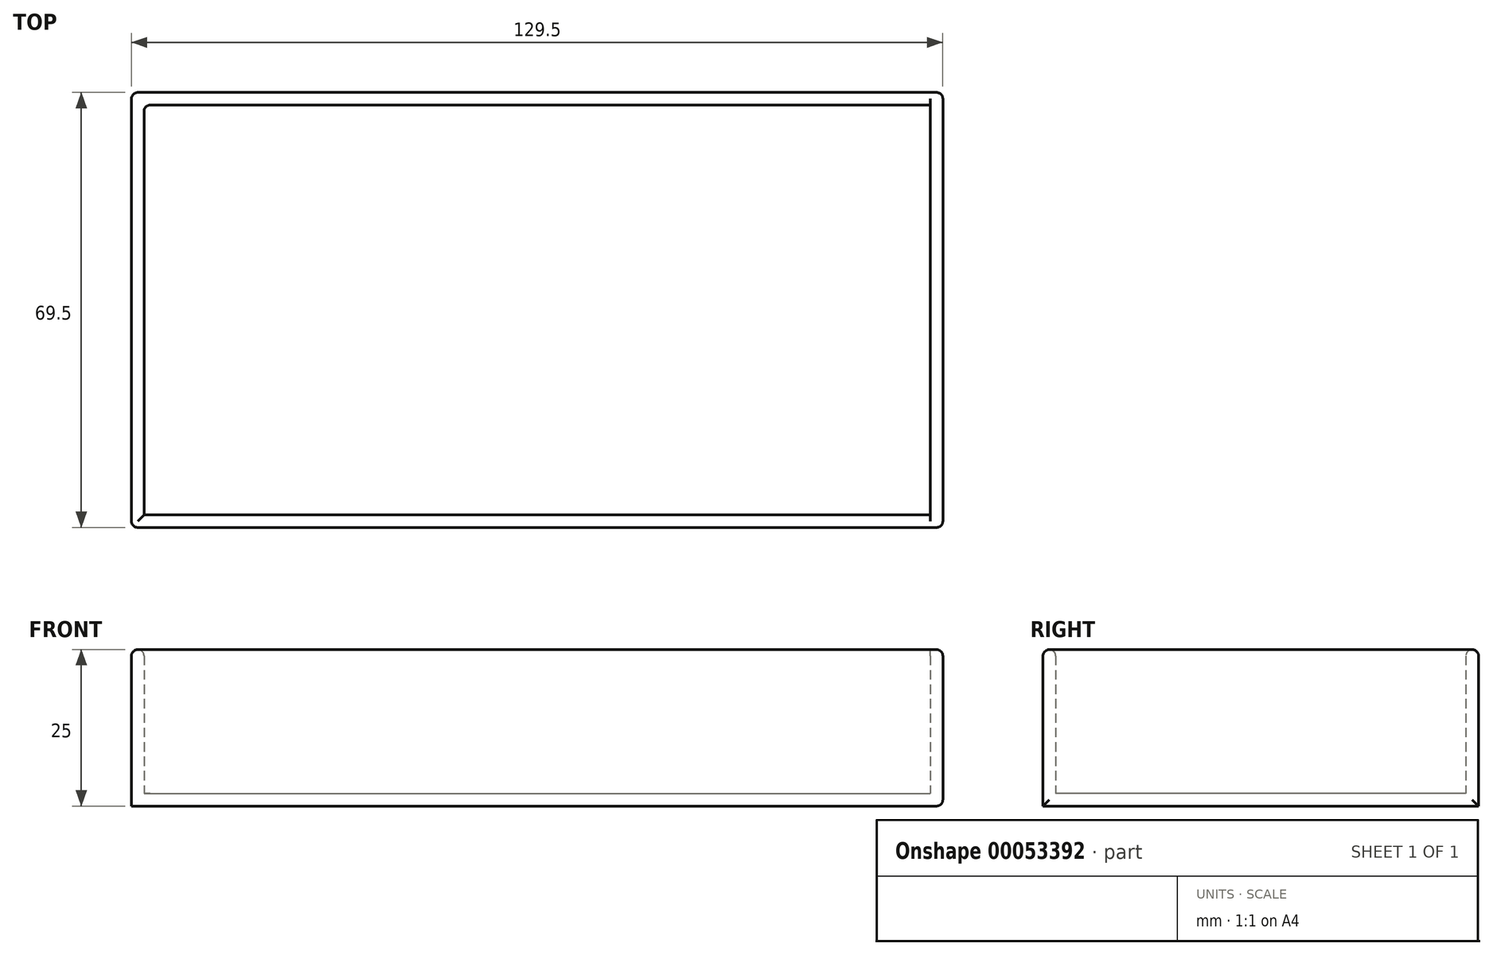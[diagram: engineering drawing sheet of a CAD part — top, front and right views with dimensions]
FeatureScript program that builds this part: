
annotation { "Feature Type Name" : "Feature", "Feature Type Description" : "" }
export const myFeature = defineFeature(function(context is Context, id is Id, definition is map)
    precondition{}
    {
        {
            var Q0;
            Q0=qCreatedBy(makeId("Top.planeOp"),FACE);
            var sketch = newSketch(context, id + "F0", { "sketchPlane" : qUnion([Q0])});
            skLineSegment(sketch, "E0.bottom", {"start": v(-56.56, 28.08) * mm, "end": v(72.94, 28.08) * mm});
            skLineSegment(sketch, "E0.top", {"start": v(-56.56, -41.42) * mm, "end": v(72.94, -41.42) * mm});
            skLineSegment(sketch, "E0.left", {"start": v(-56.56, 28.08) * mm, "end": v(-56.56, -41.42) * mm});
            skLineSegment(sketch, "E0.right", {"start": v(72.94, 28.08) * mm, "end": v(72.94, -41.42) * mm});
            skSolve(sketch);
        }
        {
            var Q0;
            Q0=makeQuery(id+"F0.imprint","IMPRINT",FACE,{"disambiguationData":[TD([[makeQuery(id+"F0.imprint","IMPRINT",EDGE,{"derivedFrom":sQuery(id+"F0.wireOp",EDGE,"E0.bottom")}),-1.0]])]});
            extrude(context, id + "F1", {"entities" : qUnion([Q0]), "depth" : 25 * mm});
        }
        {
            var Q0;
            Q0=makeQuery(id+"F1.opExtrude","CAP_FACE",FACE,{"disambiguationData":[OSD([sQuery(id+"F0.wireOp",EDGE,"E0.bottom"),sQuery(id+"F0.wireOp",EDGE,"E0.top"),sQuery(id+"F0.wireOp",EDGE,"E0.left"),sQuery(id+"F0.wireOp",EDGE,"E0.right")])],"isStart":false});
            shell(context, id + "F2", {"entities" : qUnion([Q0]), "thickness" : 2 * mm});
        }
        {
            var Q0;
            {var subQ0=sQuery(id+"F0.wireOp",EDGE,"E0.bottom");Q0=makeQuery(id+"F2.opShell","OFFSET_EDGE",EDGE,{"disambiguationData":[OSD([subQ0]),TDD([makeQuery(id+"F1.opExtrude","CAP_EDGE",EDGE,{"disambiguationData":[OSD([subQ0])],"isStart":false})])]});}
            var Q1;
            Q1=makeQuery(id+"F1.opExtrude","CAP_EDGE",EDGE,{"disambiguationData":[OSD([sQuery(id+"F0.wireOp",EDGE,"E0.left")])],"isStart":false});
            var Q2;
            {var subQ0=sQuery(id+"F0.wireOp",EDGE,"E0.left");Q2=makeQuery(id+"F2.opShell","OFFSET_EDGE",EDGE,{"disambiguationData":[OSD([subQ0]),TDD([makeQuery(id+"F1.opExtrude","CAP_EDGE",EDGE,{"disambiguationData":[OSD([subQ0])],"isStart":false})])]});}
            var Q3;
            Q3=makeQuery(id+"F1.opExtrude","CAP_EDGE",EDGE,{"disambiguationData":[OSD([sQuery(id+"F0.wireOp",EDGE,"E0.top")])],"isStart":false});
            var Q4;
            Q4=makeQuery(id+"F1.opExtrude","CAP_EDGE",EDGE,{"disambiguationData":[OSD([sQuery(id+"F0.wireOp",EDGE,"E0.right")])],"isStart":true});
            var Q5;
            Q5=makeQuery(id+"F1.opExtrude","CAP_EDGE",EDGE,{"disambiguationData":[OSD([sQuery(id+"F0.wireOp",EDGE,"E0.right")])],"isStart":false});
            var Q6;
            {var subQ0=sQuery(id+"F0.wireOp",EDGE,"E0.top");Q6=makeQuery(id+"F2.opShell","OFFSET_EDGE",EDGE,{"disambiguationData":[OSD([subQ0]),TDD([makeQuery(id+"F1.opExtrude","CAP_EDGE",EDGE,{"disambiguationData":[OSD([subQ0])],"isStart":false})])]});}
            var Q7;
            Q7=makeQuery(id+"F1.opExtrude","CAP_EDGE",EDGE,{"disambiguationData":[OSD([sQuery(id+"F0.wireOp",EDGE,"E0.bottom")])],"isStart":false});
            var Q8;
            Q8=makeQuery(id+"F1.opExtrude","SWEPT_EDGE",EDGE,{"disambiguationData":[OSD([sQuery(id+"F0.wireOp",EDGE,"E0.bottom"),sQuery(id+"F0.wireOp",EDGE,"E0.right")])]});
            var Q9;
            Q9=makeQuery(id+"F1.opExtrude","SWEPT_EDGE",EDGE,{"disambiguationData":[OSD([sQuery(id+"F0.wireOp",EDGE,"E0.bottom"),sQuery(id+"F0.wireOp",EDGE,"E0.left")])]});
            var Q10;
            Q10=makeQuery(id+"F1.opExtrude","SWEPT_EDGE",EDGE,{"disambiguationData":[OSD([sQuery(id+"F0.wireOp",EDGE,"E0.top"),sQuery(id+"F0.wireOp",EDGE,"E0.left")])]});
            var Q11;
            Q11=makeQuery(id+"F2.opShell","OFFSET_EDGE",EDGE,{"disambiguationData":[OSD([sQuery(id+"F0.wireOp",EDGE,"E0.bottom"),sQuery(id+"F0.wireOp",EDGE,"E0.left")])]});
            var Q12;
            Q12=makeQuery(id+"F1.opExtrude","SWEPT_EDGE",EDGE,{"disambiguationData":[OSD([sQuery(id+"F0.wireOp",EDGE,"E0.top"),sQuery(id+"F0.wireOp",EDGE,"E0.right")])]});
            fillet(context, id + "F3", {"entities" : qUnion([Q0, Q1, Q2, Q3, Q4, Q5, Q6, Q7, Q8, Q9, Q10, Q11, Q12]), "radius" : 1 * mm, "tangentPropagation" : true, "allowEdgeOverflow" : false});
        }
    });
